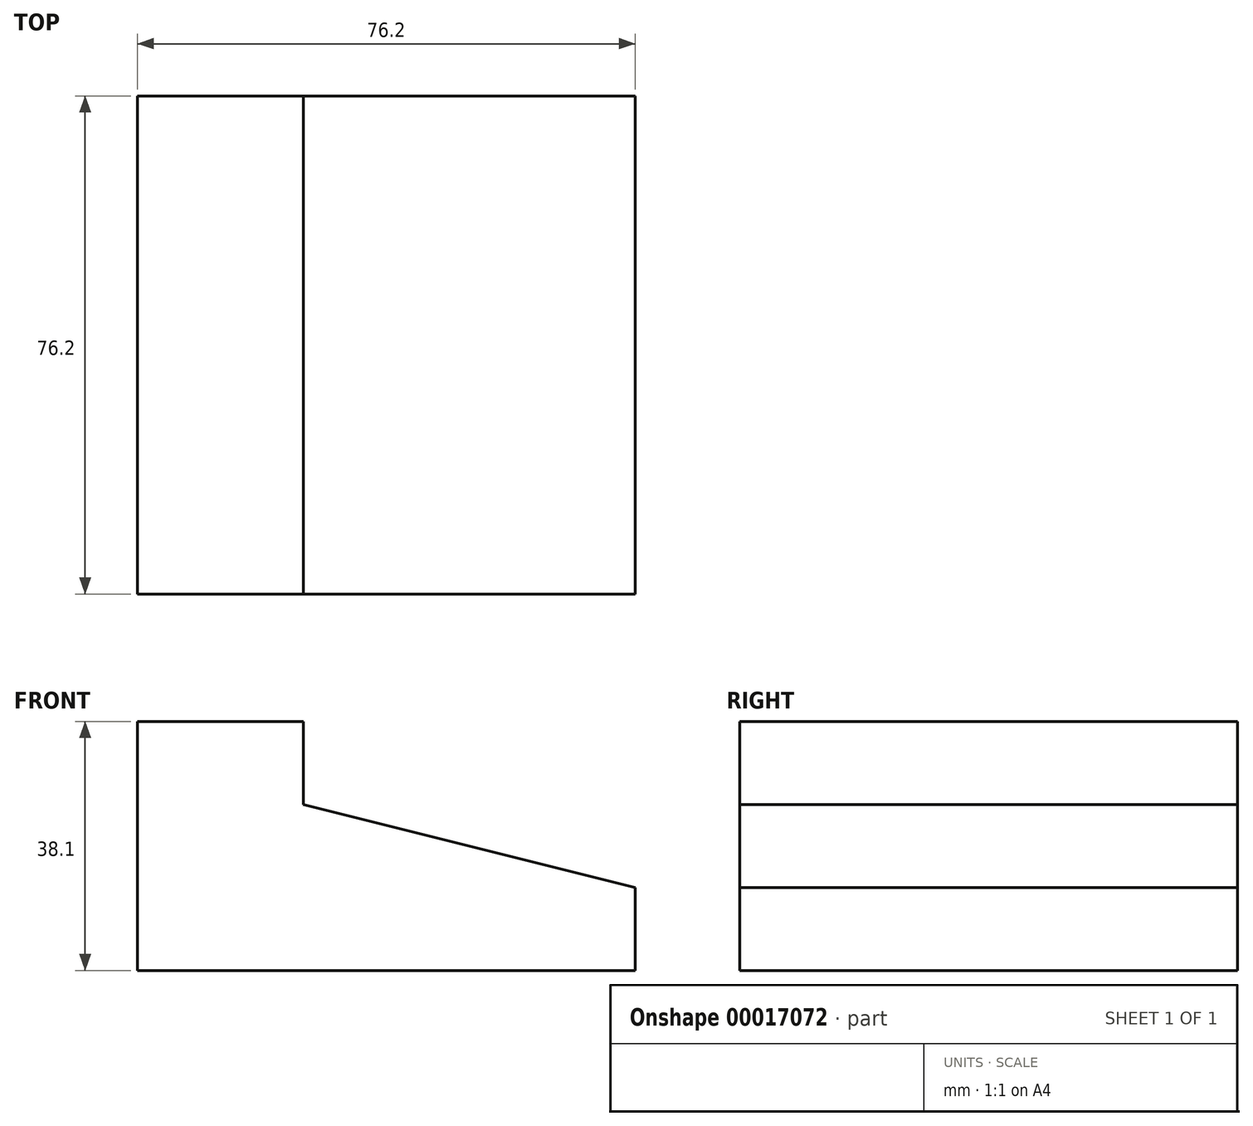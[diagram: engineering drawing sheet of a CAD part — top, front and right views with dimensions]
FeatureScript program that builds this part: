
annotation { "Feature Type Name" : "Feature", "Feature Type Description" : "" }
export const myFeature = defineFeature(function(context is Context, id is Id, definition is map)
    precondition{}
    {
        {
            var Q0;
            Q0=qCreatedBy(makeId("Front.planeOp"),FACE);
            var sketch = newSketch(context, id + "F0", { "sketchPlane" : qUnion([Q0])});
            skLineSegment(sketch, "E0", {"start": v(-44, 21.31) * mm, "end": v(-44, -16.79) * mm});
            skLineSegment(sketch, "E1", {"start": v(-44, -16.79) * mm, "end": v(32.2, -16.79) * mm});
            skLineSegment(sketch, "E2", {"start": v(32.2, -16.79) * mm, "end": v(32.2, -4.09) * mm});
            skLineSegment(sketch, "E3", {"start": v(-44, 21.31) * mm, "end": v(-18.6, 21.31) * mm});
            skLineSegment(sketch, "E4", {"start": v(-18.6, 21.31) * mm, "end": v(-18.6, 8.61) * mm});
            skLineSegment(sketch, "E5", {"start": v(-18.6, 8.61) * mm, "end": v(32.2, -4.09) * mm});
            skSolve(sketch);
        }
        {
            var Q0;
            Q0=makeQuery(id+"F0.imprint","IMPRINT",FACE,{"disambiguationData":[TD([[makeQuery(id+"F0.imprint","IMPRINT",EDGE,{"derivedFrom":sQuery(id+"F0.wireOp",EDGE,"E0")}),1.0]])]});
            extrude(context, id + "F1", {"entities" : qUnion([Q0]), "depth" : 76.2 * mm});
        }
    });
